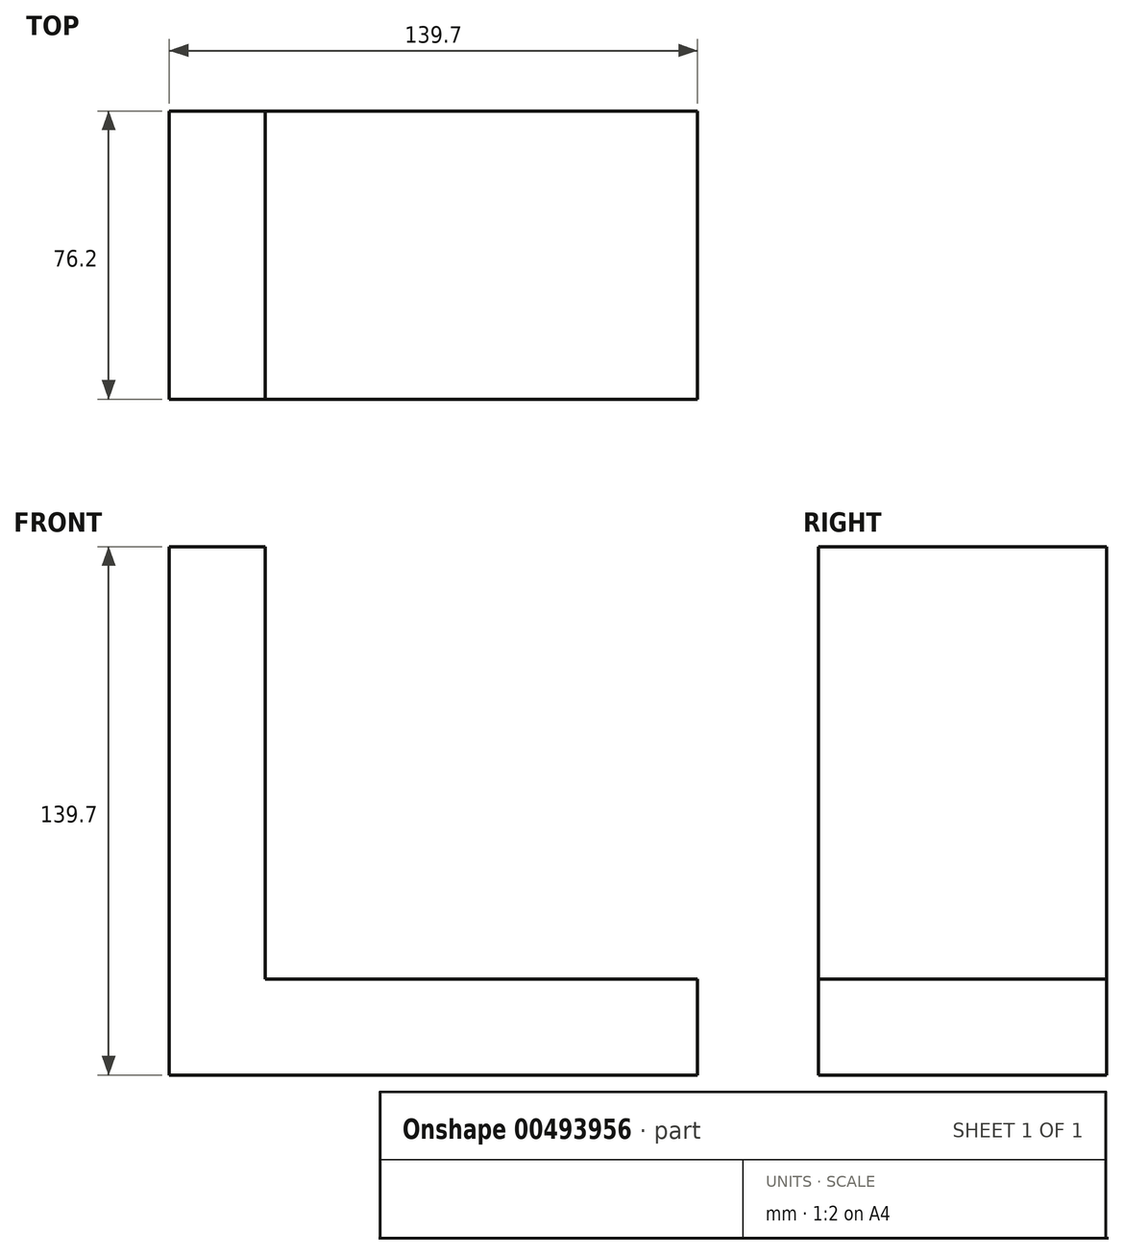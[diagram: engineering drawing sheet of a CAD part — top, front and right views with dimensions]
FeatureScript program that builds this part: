
annotation { "Feature Type Name" : "Feature", "Feature Type Description" : "" }
export const myFeature = defineFeature(function(context is Context, id is Id, definition is map)
    precondition{}
    {
        {
            var Q0;
            Q0=qCreatedBy(makeId("Front.planeOp"),FACE);
            var sketch = newSketch(context, id + "F0", { "sketchPlane" : qUnion([Q0])});
            skLineSegment(sketch, "E0", {"start": v(0, 0) * mm, "end": v(0, 114.3) * mm});
            skLineSegment(sketch, "E1", {"start": v(0, 114.3) * mm, "end": v(-25.4, 114.3) * mm});
            skLineSegment(sketch, "E2", {"start": v(-25.4, 114.3) * mm, "end": v(-25.4, -25.4) * mm});
            skLineSegment(sketch, "E3", {"start": v(-25.4, -25.4) * mm, "end": v(114.3, -25.4) * mm});
            skLineSegment(sketch, "E4", {"start": v(114.3, -25.4) * mm, "end": v(114.3, 0) * mm});
            skLineSegment(sketch, "E5", {"start": v(114.3, 0) * mm, "end": v(0, 0) * mm});
            skSolve(sketch);
        }
        {
            var Q0;
            Q0 = qSketchRegion(id + "F0", true);
            extrude(context, id + "F1", {"entities" : qUnion([Q0]), "depth" : 76.2 * mm});
        }
    });
